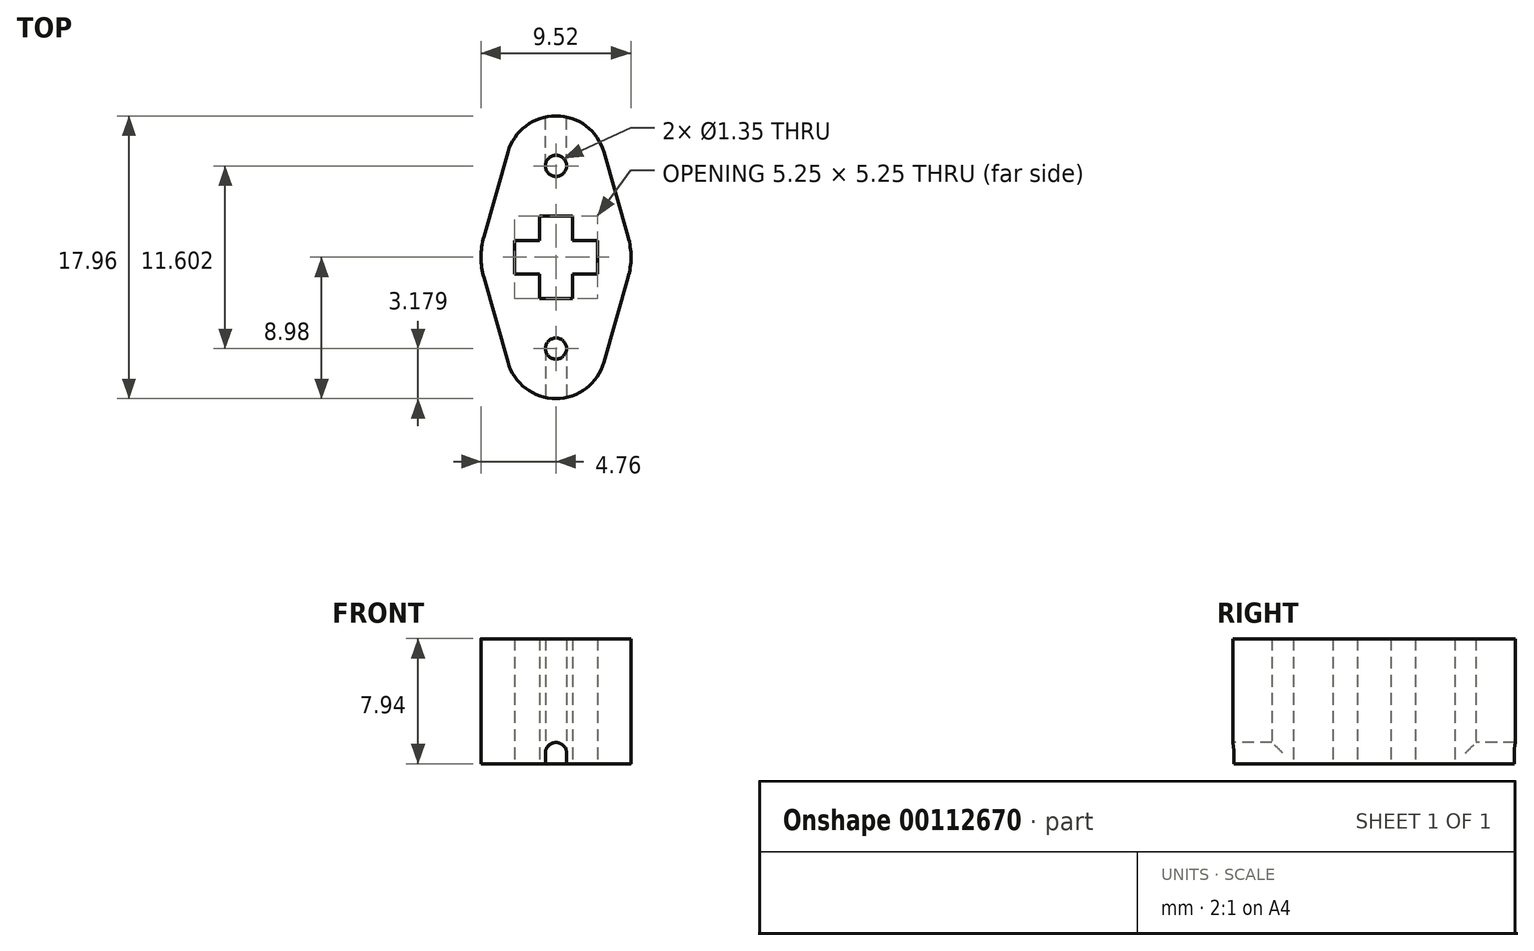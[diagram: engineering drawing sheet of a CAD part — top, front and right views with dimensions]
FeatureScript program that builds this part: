
annotation { "Feature Type Name" : "Feature", "Feature Type Description" : "" }
export const myFeature = defineFeature(function(context is Context, id is Id, definition is map)
    precondition{}
    {
        {
            var Q0;
            Q0=qCreatedBy(makeId("Top.planeOp"),FACE);
            var sketch = newSketch(context, id + "F0", { "sketchPlane" : qUnion([Q0])});
            skLineSegment(sketch, "E0.bottom", {"start": v(1.06, 2.63) * mm, "end": v(-1.06, 2.63) * mm});
            skLineSegment(sketch, "E0.top", {"start": v(1.06, -2.63) * mm, "end": v(-1.06, -2.63) * mm});
            skLineSegment(sketch, "E0.left", {"start": v(1.06, 2.63) * mm, "end": v(1.06, -2.63) * mm});
            skLineSegment(sketch, "E0.right", {"start": v(-1.06, 2.63) * mm, "end": v(-1.06, -2.63) * mm});
            skPoint(sketch, "E0.middle", {"position": v(0, 0) * mm});
            skLineSegment(sketch, "E1.bottom", {"start": v(2.63, -1.06) * mm, "end": v(-2.63, -1.06) * mm});
            skLineSegment(sketch, "E1.top", {"start": v(2.63, 1.06) * mm, "end": v(-2.63, 1.06) * mm});
            skLineSegment(sketch, "E1.left", {"start": v(2.63, -1.06) * mm, "end": v(2.63, 1.06) * mm});
            skLineSegment(sketch, "E1.right", {"start": v(-2.63, -1.06) * mm, "end": v(-2.63, 1.06) * mm});
            skLineSegment(sketch, "E2", {"start": v(-4.58, -1.3) * mm, "end": v(-3.05, -6.67) * mm});
            skLineSegment(sketch, "E3", {"start": v(4.58, -1.3) * mm, "end": v(3.05, -6.67) * mm});
            skLineSegment(sketch, "E4", {"start": v(0, 0) * mm, "end": v(0, -5.8) * mm, "construction": true});
            skArc(sketch, "E5", {"start": v(-3.05, -6.67) * mm, "mid": v(0, -8.98) * mm, "end": v(3.05, -6.67) * mm});
            skLineSegment(sketch, "E6", {"start": v(0, 0) * mm, "end": v(0, 5.8) * mm, "construction": true});
            skCircle(sketch, "E7", {"center": v(0, 5.8) * mm, "radius": 0.67 * mm});
            skCircle(sketch, "E8", {"center": v(0, -5.8) * mm, "radius": 0.67 * mm});
            skArc(sketch, "E9", {"start": v(3.05, -6.67) * mm, "mid": v(0, -2.63) * mm, "end": v(-3.05, -6.67) * mm, "construction": true});
            skArc(sketch, "E10", {"start": v(-4.58, 1.3) * mm, "mid": v(-4.76, 0) * mm, "end": v(-4.58, -1.3) * mm});
            skArc(sketch, "E11", {"start": v(4.58, -1.3) * mm, "mid": v(4.76, 0) * mm, "end": v(4.58, 1.3) * mm});
            skArc(sketch, "E12", {"start": v(3.05, 6.67) * mm, "mid": v(0, 8.98) * mm, "end": v(-3.05, 6.67) * mm});
            skLineSegment(sketch, "E13", {"start": v(-4.58, 1.3) * mm, "end": v(-3.05, 6.67) * mm});
            skLineSegment(sketch, "E14", {"start": v(4.58, 1.3) * mm, "end": v(3.05, 6.67) * mm});
            skSolve(sketch);
        }
        {
            var Q0;
            Q0=qSketchRegion(id+"F0",true);
            extrude(context, id + "F1", {"entities" : qUnion([Q0]), "depth" : 7.94 * mm});
        }
        {
            var Q0;
            Q0=makeQuery(id+"F1.opExtrude","CAP_FACE",FACE,{"disambiguationData":[OSD([sQuery(id+"F0.wireOp",EDGE,"E0.bottom"),sQuery(id+"F0.wireOp",EDGE,"E0.top"),sQuery(id+"F0.wireOp",EDGE,"E0.left"),sQuery(id+"F0.wireOp",EDGE,"E0.right"),sQuery(id+"F0.wireOp",EDGE,"E1.bottom"),sQuery(id+"F0.wireOp",EDGE,"E1.top"),sQuery(id+"F0.wireOp",EDGE,"E1.left"),sQuery(id+"F0.wireOp",EDGE,"E1.right"),sQuery(id+"F0.wireOp",EDGE,"E2"),sQuery(id+"F0.wireOp",EDGE,"E3"),sQuery(id+"F0.wireOp",EDGE,"E5"),sQuery(id+"F0.wireOp",EDGE,"E7"),sQuery(id+"F0.wireOp",EDGE,"E8"),sQuery(id+"F0.wireOp",EDGE,"E10"),sQuery(id+"F0.wireOp",EDGE,"E11"),sQuery(id+"F0.wireOp",EDGE,"E12"),sQuery(id+"F0.wireOp",EDGE,"E13"),sQuery(id+"F0.wireOp",EDGE,"E14")])],"isStart":true});
            var sketch = newSketch(context, id + "F2", { "sketchPlane" : qUnion([Q0])});
            skLineSegment(sketch, "E15.bottom", {"start": v(0.67, 5.8) * mm, "end": v(-0.67, 5.8) * mm});
            skLineSegment(sketch, "E15.top", {"start": v(0.67, 8.9) * mm, "end": v(-0.67, 8.9) * mm, "construction": true});
            skLineSegment(sketch, "E15.left", {"start": v(0.67, 5.8) * mm, "end": v(0.67, 8.9) * mm});
            skLineSegment(sketch, "E15.right", {"start": v(-0.67, 5.8) * mm, "end": v(-0.67, 8.9) * mm});
            skPoint(sketch, "E16", {"position": v(0, 5.8) * mm});
            skArc(sketch, "E17", {"start": v(0.67, 8.9) * mm, "mid": v(0, 8.98) * mm, "end": v(-0.67, 8.9) * mm});
            skLineSegment(sketch, "E18.bottom", {"start": v(0.67, -5.8) * mm, "end": v(-0.67, -5.8) * mm});
            skLineSegment(sketch, "E18.top", {"start": v(0.67, -8.9) * mm, "end": v(-0.67, -8.9) * mm, "construction": true});
            skLineSegment(sketch, "E18.left", {"start": v(0.67, -5.8) * mm, "end": v(0.67, -8.9) * mm});
            skLineSegment(sketch, "E18.right", {"start": v(-0.67, -5.8) * mm, "end": v(-0.67, -8.9) * mm});
            skArc(sketch, "E19", {"start": v(-0.67, -8.9) * mm, "mid": v(0, -8.98) * mm, "end": v(0.67, -8.9) * mm});
            skSolve(sketch);
        }
        {
            var Q0;
            Q0 = qSketchRegion(id + "F2", true);
            extrude(context, id + "F3", {"entities" : qUnion([Q0]), "operationType" : NewBodyOperationType.REMOVE, "oppositeDirection" : true, "depth" : 1.35 * mm});
        }
        {
            var Q0;
            Q0=makeQuery(id+"F3.boolean.opBoolean","COPY",EDGE,{"derivedFrom":makeQuery(id+"F3.opExtrude","CAP_EDGE",EDGE,{"disambiguationData":[OSD([sQuery(id+"F2.wireOp",EDGE,"E18.left")])],"isStart":false})});
            var Q1;
            Q1=makeQuery(id+"F3.boolean.opBoolean","COPY",EDGE,{"derivedFrom":makeQuery(id+"F3.opExtrude","CAP_EDGE",EDGE,{"disambiguationData":[OSD([sQuery(id+"F2.wireOp",EDGE,"E18.right")])],"isStart":false})});
            var Q2;
            Q2=makeQuery(id+"F3.boolean.opBoolean","COPY",EDGE,{"derivedFrom":makeQuery(id+"F3.opExtrude","CAP_EDGE",EDGE,{"disambiguationData":[OSD([sQuery(id+"F2.wireOp",EDGE,"E15.left")])],"isStart":false})});
            var Q3;
            Q3=makeQuery(id+"F3.boolean.opBoolean","COPY",EDGE,{"derivedFrom":makeQuery(id+"F3.opExtrude","CAP_EDGE",EDGE,{"disambiguationData":[OSD([sQuery(id+"F2.wireOp",EDGE,"E15.right")])],"isStart":false})});
            fillet(context, id + "F4", {"entities" : qUnion([Q0, Q1, Q2, Q3]), "radius" : 0.67 * mm, "tangentPropagation" : true, "allowEdgeOverflow" : false});
        }
    });
